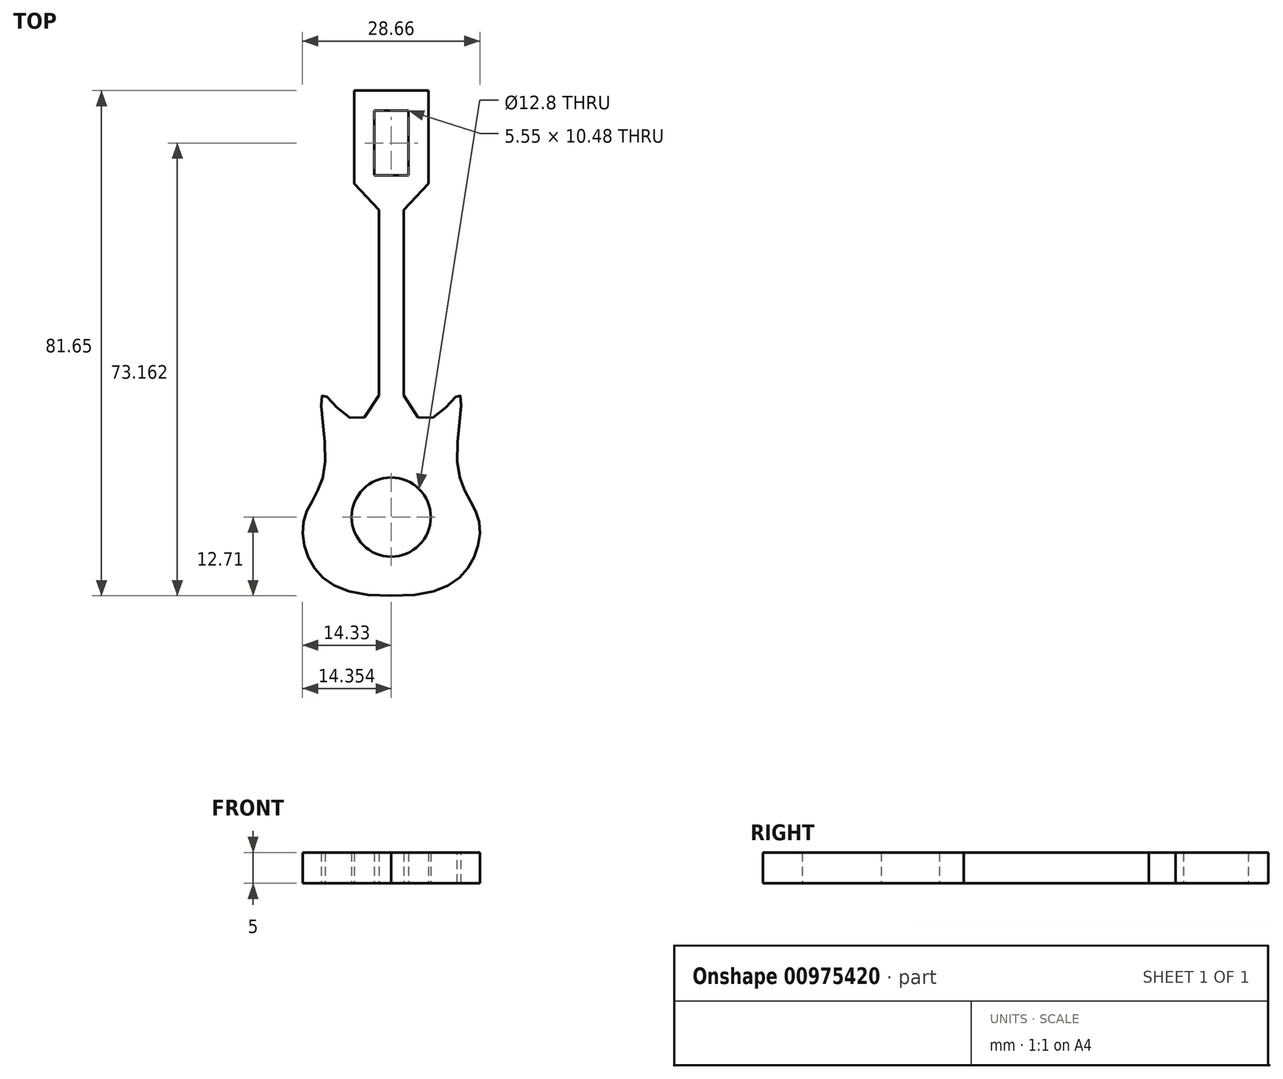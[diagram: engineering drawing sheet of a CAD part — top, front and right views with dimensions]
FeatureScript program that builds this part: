
annotation { "Feature Type Name" : "Feature", "Feature Type Description" : "" }
export const myFeature = defineFeature(function(context is Context, id is Id, definition is map)
    precondition{}
    {
        {
            var Q0;
            Q0=qCreatedBy(makeId("Top.planeOp"),FACE);
            var sketch = newSketch(context, id + "F0", { "sketchPlane" : qUnion([Q0])});
            skLineSegment(sketch, "E0", {"start": v(-6, 68.94) * mm, "end": v(0, 68.94) * mm});
            skLineSegment(sketch, "E1", {"start": v(-6, 68.94) * mm, "end": v(-6, 53.94) * mm});
            skLineSegment(sketch, "E2", {"start": v(-6, 53.94) * mm, "end": v(-2, 49.67) * mm});
            skLineSegment(sketch, "E3", {"start": v(-2, 49.67) * mm, "end": v(-2, 19.67) * mm});
            skPoint(sketch, "E4.1.internal.orphan", {"position": v(-10.7, 19.67) * mm});
            skPoint(sketch, "E4.12.internal.orphan", {"position": v(0, -45.38) * mm});
            skPoint(sketch, "E4.3.internal.orphan", {"position": v(-23.64, 0) * mm});
            skPoint(sketch, "E4.endDerivative.orphan", {"position": v(0, -33.06) * mm});
            skFitSpline(sketch, "E5", {"points": [v(-2, 19.67) * mm, v(-10.7, 19.67) * mm, v(-10.7, 8.55) * mm, v(-14, 0) * mm, v(-12.85, -7.56) * mm, v(0, -12.7) * mm], "startDerivative": vector(-51.5, -133.27) * mm, "endDerivative": vector(96.43, 1.95) * mm});
            skPoint(sketch, "E6.MirrorCS.end.orphan", {"position": v(-2, 118.2) * mm});
            skPoint(sketch, "E6.MirrorCS.start.orphan", {"position": v(-2, 88.2) * mm});
            skPoint(sketch, "E7.MirrorCS.start.orphan", {"position": v(-6, 83.94) * mm});
            skPoint(sketch, "E8.MirrorCS.start.orphan", {"position": v(-6, 68.94) * mm});
            skLineSegment(sketch, "E9.MirrorCS", {"start": v(6, 68.94) * mm, "end": v(0, 68.94) * mm});
            skLineSegment(sketch, "E10.MirrorCS", {"start": v(6, 68.94) * mm, "end": v(6, 53.94) * mm});
            skLineSegment(sketch, "E11.MirrorCS", {"start": v(6, 53.94) * mm, "end": v(2, 49.67) * mm});
            skLineSegment(sketch, "E12.MirrorCS", {"start": v(2, 49.67) * mm, "end": v(2, 19.67) * mm});
            skFitSpline(sketch, "E13.MirrorCS", {"points": [v(2, 19.67) * mm, v(10.7, 19.67) * mm, v(10.7, 8.55) * mm, v(14, 0) * mm, v(12.85, -7.56) * mm, v(0, -12.7) * mm], "startDerivative": vector(51.5, -133.27) * mm, "endDerivative": vector(-96.43, 1.95) * mm});
            skCircle(sketch, "E14", {"center": v(0, 0) * mm, "radius": 6.4 * mm});
            skLineSegment(sketch, "E15.bottom", {"start": v(-2.75, 65.7) * mm, "end": v(2.8, 65.7) * mm});
            skLineSegment(sketch, "E15.top", {"start": v(-2.75, 55.21) * mm, "end": v(2.8, 55.21) * mm});
            skLineSegment(sketch, "E15.left", {"start": v(-2.75, 65.7) * mm, "end": v(-2.75, 55.21) * mm});
            skLineSegment(sketch, "E15.right", {"start": v(2.8, 65.7) * mm, "end": v(2.8, 55.21) * mm});
            skSolve(sketch);
        }
        {
            var Q0;
            Q0=makeQuery(id+"F0.imprint","IMPRINT",FACE,{"disambiguationData":[TD([[makeQuery(id+"F0.imprint","IMPRINT",EDGE,{"derivedFrom":sQuery(id+"F0.wireOp",EDGE,"E0")}),-1.0]])]});
            extrude(context, id + "F1", {"entities" : qUnion([Q0]), "depth" : 5 * mm, "offsetDistance" : 25 * mm});
        }
    });
